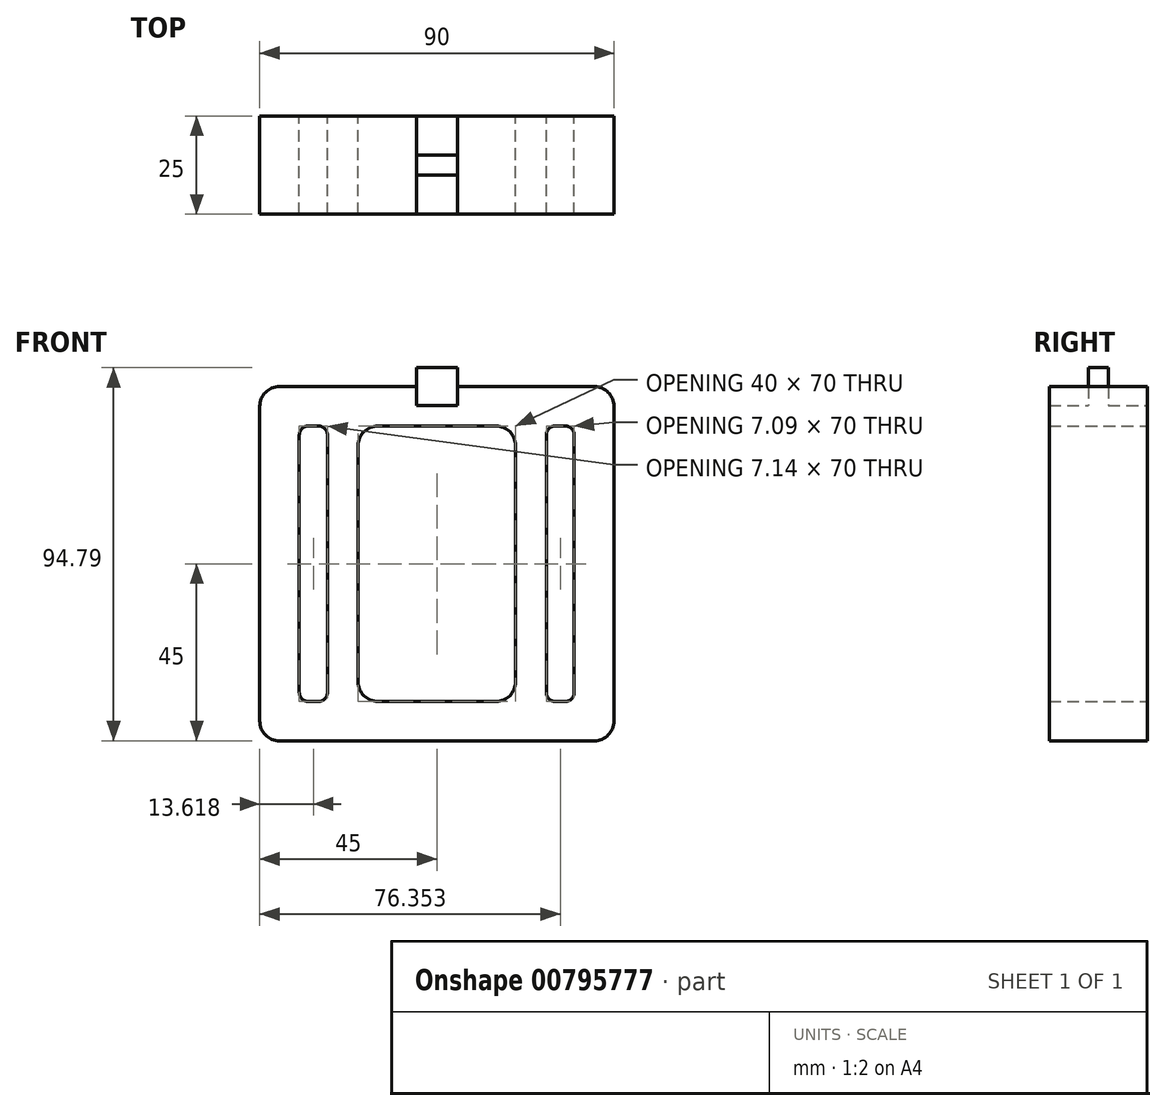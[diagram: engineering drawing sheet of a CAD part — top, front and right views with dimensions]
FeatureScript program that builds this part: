
annotation { "Feature Type Name" : "Feature", "Feature Type Description" : "" }
export const myFeature = defineFeature(function(context is Context, id is Id, definition is map)
    precondition{}
    {
        {
            var Q0;
            Q0=qCreatedBy(makeId("Front.planeOp"),FACE);
            var sketch = newSketch(context, id + "F0", { "sketchPlane" : qUnion([Q0])});
            skLineSegment(sketch, "E0.bottom", {"start": v(-40, 45) * mm, "end": v(40, 45) * mm});
            skLineSegment(sketch, "E0.top", {"start": v(-40, -45) * mm, "end": v(40, -45) * mm});
            skLineSegment(sketch, "E0.left", {"start": v(-45, 40) * mm, "end": v(-45, -40) * mm});
            skLineSegment(sketch, "E0.right", {"start": v(45, 40) * mm, "end": v(45, -40) * mm});
            skPoint(sketch, "E0.middle", {"position": v(0, 0) * mm});
            skLineSegment(sketch, "E1.bottom", {"start": v(8.35, 35) * mm, "end": v(15, 35) * mm});
            skLineSegment(sketch, "E1.top", {"start": v(8.35, -35) * mm, "end": v(15, -35) * mm});
            skLineSegment(sketch, "E1.left", {"start": v(-20, 30) * mm, "end": v(-20, -30) * mm});
            skLineSegment(sketch, "E1.right", {"start": v(20, 30) * mm, "end": v(20, -30) * mm});
            skLineSegment(sketch, "E2.bottom", {"start": v(-15, 35) * mm, "end": v(-8.35, 35) * mm});
            skLineSegment(sketch, "E2.top", {"start": v(-15, -35) * mm, "end": v(-8.35, -35) * mm});
            skLineSegment(sketch, "E2.left", {"start": v(-34.95, 32.75) * mm, "end": v(-34.95, -32.75) * mm});
            skLineSegment(sketch, "E2.right", {"start": v(34.9, 32.75) * mm, "end": v(34.9, -32.75) * mm});
            skLineSegment(sketch, "E3.bottom", {"start": v(-3.35, 35) * mm, "end": v(3.35, 35) * mm});
            skLineSegment(sketch, "E3.top", {"start": v(-3.35, -35) * mm, "end": v(3.35, -35) * mm});
            skLineSegment(sketch, "E3.left", {"start": v(-3.35, 30) * mm, "end": v(-3.35, -30) * mm});
            skLineSegment(sketch, "E3.right", {"start": v(3.35, 30) * mm, "end": v(3.35, -30) * mm});
            skPoint(sketch, "E4.newPointA", {"position": v(-20, 35) * mm});
            skPoint(sketch, "E4.newPointB", {"position": v(-35, 35) * mm});
            skArc(sketch, "E4.filletArc", {"start": v(-15, 35) * mm, "mid": v(-18.54, 33.54) * mm, "end": v(-20, 30) * mm});
            skPoint(sketch, "E5.newPointB", {"position": v(35, 35) * mm});
            skArc(sketch, "E5.filletArc", {"start": v(-3.35, 30) * mm, "mid": v(-4.82, 33.54) * mm, "end": v(-8.35, 35) * mm});
            skArc(sketch, "E6.filletArc", {"start": v(8.35, 35) * mm, "mid": v(4.82, 33.54) * mm, "end": v(3.35, 30) * mm});
            skPoint(sketch, "E7.visualSharp", {"position": v(20, 35) * mm});
            skArc(sketch, "E7.filletArc", {"start": v(20, 30) * mm, "mid": v(18.54, 33.54) * mm, "end": v(15, 35) * mm});
            skPoint(sketch, "E8.newPointA", {"position": v(-20, -35) * mm});
            skPoint(sketch, "E8.newPointB", {"position": v(-35, -35) * mm});
            skArc(sketch, "E8.filletArc", {"start": v(-20, -30) * mm, "mid": v(-18.54, -33.54) * mm, "end": v(-15, -35) * mm});
            skPoint(sketch, "E9.newPointB", {"position": v(35, -35) * mm});
            skArc(sketch, "E9.filletArc", {"start": v(-8.35, -35) * mm, "mid": v(-4.82, -33.54) * mm, "end": v(-3.35, -30) * mm});
            skArc(sketch, "E10.filletArc", {"start": v(3.35, -30) * mm, "mid": v(4.82, -33.54) * mm, "end": v(8.35, -35) * mm});
            skPoint(sketch, "E11.visualSharp", {"position": v(20, -35) * mm});
            skArc(sketch, "E11.filletArc", {"start": v(15, -35) * mm, "mid": v(18.54, -33.54) * mm, "end": v(20, -30) * mm});
            skPoint(sketch, "E12.visualSharp", {"position": v(45, 45) * mm});
            skArc(sketch, "E12.filletArc", {"start": v(45, 40) * mm, "mid": v(43.54, 43.54) * mm, "end": v(40, 45) * mm});
            skPoint(sketch, "E13.visualSharp", {"position": v(45, -45) * mm});
            skArc(sketch, "E13.filletArc", {"start": v(40, -45) * mm, "mid": v(43.54, -43.54) * mm, "end": v(45, -40) * mm});
            skPoint(sketch, "E14.visualSharp", {"position": v(-45, -45) * mm});
            skArc(sketch, "E14.filletArc", {"start": v(-45, -40) * mm, "mid": v(-43.54, -43.54) * mm, "end": v(-40, -45) * mm});
            skPoint(sketch, "E15.visualSharp", {"position": v(-45, 45) * mm});
            skArc(sketch, "E15.filletArc", {"start": v(-40, 45) * mm, "mid": v(-43.54, 43.54) * mm, "end": v(-45, 40) * mm});
            skLineSegment(sketch, "E16.bottom", {"start": v(-27.81, 35) * mm, "end": v(27.81, 35) * mm});
            skLineSegment(sketch, "E16.top", {"start": v(-27.81, -35) * mm, "end": v(27.81, -35) * mm});
            skLineSegment(sketch, "E16.left", {"start": v(-27.81, 32.75) * mm, "end": v(-27.81, -32.75) * mm});
            skLineSegment(sketch, "E16.right", {"start": v(27.81, 32.75) * mm, "end": v(27.81, -32.75) * mm});
            skLineSegment(sketch, "E17", {"start": v(-32.7, 35) * mm, "end": v(-27.81, 35) * mm});
            skLineSegment(sketch, "E18", {"start": v(-32.7, -35) * mm, "end": v(-30.06, -35) * mm});
            skLineSegment(sketch, "E19", {"start": v(30.06, -35) * mm, "end": v(32.64, -35) * mm});
            skLineSegment(sketch, "E20", {"start": v(27.81, 35) * mm, "end": v(32.64, 35) * mm});
            skPoint(sketch, "E21.visualSharp", {"position": v(-34.95, 35) * mm});
            skArc(sketch, "E21.filletArc", {"start": v(-32.7, 35) * mm, "mid": v(-34.3, 34.34) * mm, "end": v(-34.95, 32.75) * mm});
            skPoint(sketch, "E22.visualSharp", {"position": v(34.9, 35) * mm});
            skArc(sketch, "E22.filletArc", {"start": v(34.9, 32.75) * mm, "mid": v(34.24, 34.34) * mm, "end": v(32.64, 35) * mm});
            skPoint(sketch, "E23.visualSharp", {"position": v(34.9, -35) * mm});
            skArc(sketch, "E23.filletArc", {"start": v(32.64, -35) * mm, "mid": v(34.24, -34.34) * mm, "end": v(34.9, -32.75) * mm});
            skPoint(sketch, "E24.visualSharp", {"position": v(-34.95, -35) * mm});
            skArc(sketch, "E24.filletArc", {"start": v(-34.95, -32.75) * mm, "mid": v(-34.3, -34.34) * mm, "end": v(-32.7, -35) * mm});
            skLineSegment(sketch, "E25", {"start": v(-32.7, 35) * mm, "end": v(-30.06, 35) * mm});
            skPoint(sketch, "E26.visualSharp", {"position": v(-27.81, 35) * mm});
            skArc(sketch, "E26.filletArc", {"start": v(-27.81, 32.75) * mm, "mid": v(-28.47, 34.34) * mm, "end": v(-30.06, 35) * mm});
            skLineSegment(sketch, "E27", {"start": v(-32.7, -35) * mm, "end": v(-27.81, -35) * mm});
            skPoint(sketch, "E28.visualSharp", {"position": v(-27.81, -35) * mm});
            skArc(sketch, "E28.filletArc", {"start": v(-30.06, -35) * mm, "mid": v(-28.47, -34.34) * mm, "end": v(-27.81, -32.75) * mm});
            skLineSegment(sketch, "E29", {"start": v(30.06, 35) * mm, "end": v(32.64, 35) * mm});
            skPoint(sketch, "E30.visualSharp", {"position": v(27.81, 35) * mm});
            skArc(sketch, "E30.filletArc", {"start": v(30.06, 35) * mm, "mid": v(28.47, 34.34) * mm, "end": v(27.81, 32.75) * mm});
            skLineSegment(sketch, "E31", {"start": v(27.81, -35) * mm, "end": v(32.64, -35) * mm});
            skPoint(sketch, "E32.visualSharp", {"position": v(27.81, -35) * mm});
            skArc(sketch, "E32.filletArc", {"start": v(27.81, -32.75) * mm, "mid": v(28.47, -34.34) * mm, "end": v(30.06, -35) * mm});
            skLineSegment(sketch, "E33.bottom", {"start": v(-5.22, 49.79) * mm, "end": v(5.22, 49.79) * mm});
            skLineSegment(sketch, "E33.top", {"start": v(-5.22, 40.21) * mm, "end": v(5.22, 40.21) * mm});
            skLineSegment(sketch, "E33.left", {"start": v(-5.22, 49.79) * mm, "end": v(-5.22, 40.21) * mm});
            skLineSegment(sketch, "E33.right", {"start": v(5.22, 49.79) * mm, "end": v(5.22, 40.21) * mm});
            skPoint(sketch, "E33.middle", {"position": v(0, 45) * mm});
            skLineSegment(sketch, "E34", {"start": v(0, 45) * mm, "end": v(0, 54.7) * mm});
            skLineSegment(sketch, "E35", {"start": v(0, 35) * mm, "end": v(0, -35) * mm});
            skSolve(sketch);
        }
        {
            var Q0;
            {var subQ0=sQuery(id+"F0.wireOp",EDGE,"E34");var subQ1=sQuery(id+"F0.wireOp",EDGE,"E0.bottom");var subQ2=makeQuery(id+"F0.imprint","INTERSECT",VERTEX,{"derivedFrom":[subQ1,subQ0]});Q0=makeQuery(id+"F0.imprint","IMPRINT",FACE,{"disambiguationData":[TD([[makeQuery(id+"F0.imprint","IMPRINT",EDGE,{"disambiguationData":[TD([[subQ2,1.0]])],"derivedFrom":subQ1}),1.0]])]});}
            var Q1;
            {var subQ0=sQuery(id+"F0.wireOp",EDGE,"E34");var subQ1=sQuery(id+"F0.wireOp",EDGE,"E0.bottom");var subQ2=makeQuery(id+"F0.imprint","INTERSECT",VERTEX,{"derivedFrom":[subQ1,subQ0]});Q1=makeQuery(id+"F0.imprint","IMPRINT",FACE,{"disambiguationData":[TD([[makeQuery(id+"F0.imprint","IMPRINT",EDGE,{"disambiguationData":[TD([[subQ2,-1.0]])],"derivedFrom":subQ1}),1.0]])]});}
            var Q2;
            {var subQ1=sQuery(id+"F0.wireOp",EDGE,"E33.top");Q2=makeQuery(id+"F0.imprint","IMPRINT",FACE,{"disambiguationData":[TD([[makeQuery(id+"F0.imprint","IMPRINT",EDGE,{"derivedFrom":subQ1}),1.0]])]});}
            extrude(context, id + "F1", {"entities" : qUnion([Q0, Q1, Q2]), "endBound" : BoundingType.SYMMETRIC, "depth" : 5 * mm, "offsetDistance" : 25 * mm});
        }
        {
            var Q0;
            Q0=makeQuery(id+"F0.imprint","IMPRINT",FACE,{"disambiguationData":[TD([[makeQuery(id+"F0.imprint","IMPRINT",EDGE,{"derivedFrom":sQuery(id+"F0.wireOp",EDGE,"E0.top")}),1.0]])]});
            var Q1;
            Q1=makeQuery(id+"F0.imprint","IMPRINT",FACE,{"disambiguationData":[TD([[makeQuery(id+"F0.imprint","IMPRINT",EDGE,{"derivedFrom":sQuery(id+"F0.wireOp",EDGE,"E1.left")}),-1.0]])]});
            var Q2;
            Q2=makeQuery(id+"F0.imprint","IMPRINT",FACE,{"disambiguationData":[TD([[makeQuery(id+"F0.imprint","IMPRINT",EDGE,{"derivedFrom":sQuery(id+"F0.wireOp",EDGE,"E1.right")}),1.0]])]});
            extrude(context, id + "F2", {"entities" : qUnion([Q0, Q1, Q2]), "operationType" : NewBodyOperationType.ADD, "endBound" : BoundingType.SYMMETRIC, "depth" : 25 * mm, "offsetDistance" : 25 * mm});
        }
    });
